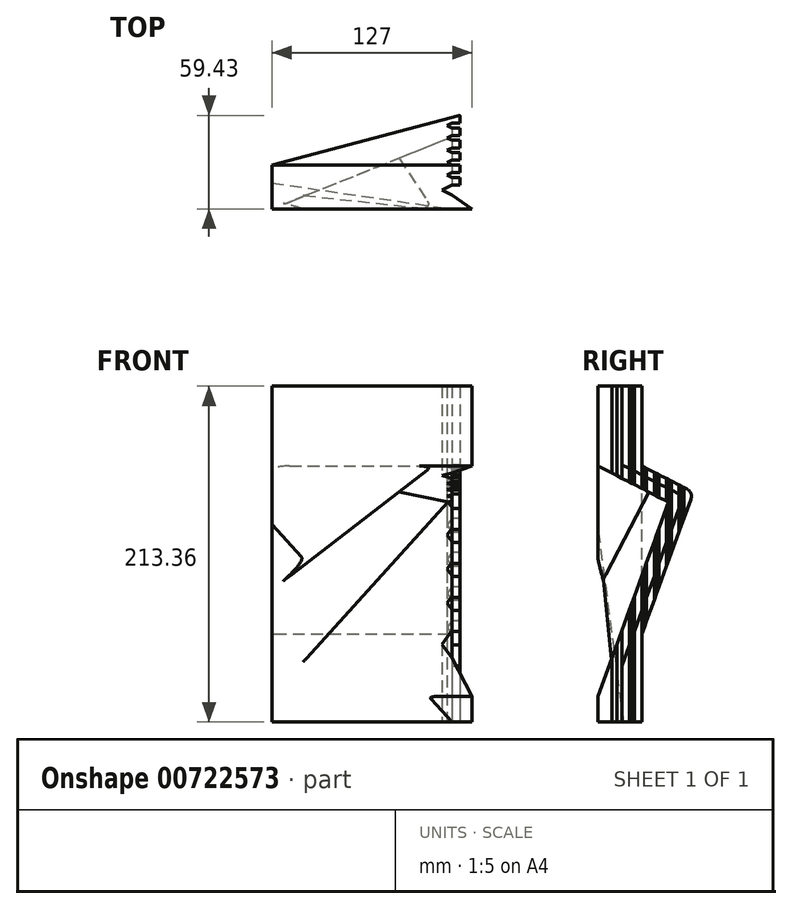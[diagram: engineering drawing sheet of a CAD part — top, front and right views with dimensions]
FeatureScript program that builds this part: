
annotation { "Feature Type Name" : "Feature", "Feature Type Description" : "" }
export const myFeature = defineFeature(function(context is Context, id is Id, definition is map)
    precondition{}
    {
        {
            var Q0;
            Q0=qCreatedBy(makeId("Top.planeOp"),FACE);
            var sketch = newSketch(context, id + "F0", { "sketchPlane" : qUnion([Q0])});
            skLineSegment(sketch, "E0", {"start": v(0, 6.35) * mm, "end": v(5.08, 6.35) * mm});
            skLineSegment(sketch, "E1", {"start": v(5.08, 6.35) * mm, "end": v(5.08, 11.18) * mm});
            skLineSegment(sketch, "E2", {"start": v(5.08, 11.18) * mm, "end": v(0, 11.18) * mm});
            skLineSegment(sketch, "E3", {"start": v(0, 11.18) * mm, "end": v(0, 14.22) * mm});
            skLineSegment(sketch, "E4", {"start": v(0, 14.22) * mm, "end": v(5.08, 14.22) * mm});
            skLineSegment(sketch, "E5", {"start": v(5.08, 14.22) * mm, "end": v(5.08, 19.05) * mm});
            skLineSegment(sketch, "E6", {"start": v(5.08, 19.05) * mm, "end": v(0, 19.05) * mm});
            skLineSegment(sketch, "E7", {"start": v(0, 19.05) * mm, "end": v(0, 22.1) * mm});
            skLineSegment(sketch, "E8", {"start": v(0, 22.1) * mm, "end": v(5.08, 22.1) * mm});
            skLineSegment(sketch, "E9", {"start": v(5.08, 22.1) * mm, "end": v(5.08, 26.92) * mm});
            skLineSegment(sketch, "E10", {"start": v(5.08, 26.92) * mm, "end": v(0, 26.92) * mm});
            skLineSegment(sketch, "E11", {"start": v(0, 26.92) * mm, "end": v(0, 29.97) * mm});
            skLineSegment(sketch, "E12", {"start": v(0, 29.97) * mm, "end": v(5.08, 29.97) * mm});
            skLineSegment(sketch, "E13", {"start": v(5.08, 29.97) * mm, "end": v(5.08, 34.8) * mm});
            skLineSegment(sketch, "E14", {"start": v(5.08, 34.8) * mm, "end": v(0, 34.8) * mm});
            skLineSegment(sketch, "E15", {"start": v(0, 34.8) * mm, "end": v(0, 37.85) * mm});
            skLineSegment(sketch, "E16", {"start": v(0, 37.85) * mm, "end": v(5.08, 37.85) * mm});
            skLineSegment(sketch, "E17", {"start": v(5.08, 37.85) * mm, "end": v(5.08, 42.67) * mm});
            skLineSegment(sketch, "E18", {"start": v(5.08, 42.67) * mm, "end": v(0, 42.67) * mm});
            skLineSegment(sketch, "E19", {"start": v(-114.3, 0) * mm, "end": v(0, 0) * mm});
            skLineSegment(sketch, "E20", {"start": v(0, 0) * mm, "end": v(0, 6.35) * mm});
            skLineSegment(sketch, "E21", {"start": v(0, 42.67) * mm, "end": v(0, 45.72) * mm});
            skLineSegment(sketch, "E22", {"start": v(-114.3, 53.6) * mm, "end": v(-114.3, 0) * mm});
            skLineSegment(sketch, "E23", {"start": v(0, 45.72) * mm, "end": v(5.08, 45.72) * mm});
            skLineSegment(sketch, "E24", {"start": v(5.08, 45.72) * mm, "end": v(5.08, 50.55) * mm});
            skLineSegment(sketch, "E25", {"start": v(5.08, 50.55) * mm, "end": v(0, 50.55) * mm});
            skLineSegment(sketch, "E26", {"start": v(0, 50.55) * mm, "end": v(0, 53.6) * mm});
            skLineSegment(sketch, "E27", {"start": v(0, 53.6) * mm, "end": v(-114.3, 53.6) * mm});
            skLineSegment(sketch, "E28", {"start": v(0, 0) * mm, "end": v(0, -8.89) * mm});
            skLineSegment(sketch, "E29", {"start": v(0, -8.89) * mm, "end": v(-114.3, -8.9) * mm});
            skLineSegment(sketch, "E30", {"start": v(-114.3, -8.9) * mm, "end": v(-114.3, 0) * mm});
            skLineSegment(sketch, "E31", {"start": v(0, -8.89) * mm, "end": v(12.7, -8.89) * mm});
            skLineSegment(sketch, "E32", {"start": v(12.7, -8.89) * mm, "end": v(0, 0) * mm});
            skLineSegment(sketch, "E33", {"start": v(0, 0) * mm, "end": v(-6.35, 3.17) * mm});
            skLineSegment(sketch, "E34", {"start": v(-6.35, 3.18) * mm, "end": v(0, 6.35) * mm});
            skLineSegment(sketch, "E35", {"start": v(0, 11.18) * mm, "end": v(-3.05, 12.7) * mm});
            skLineSegment(sketch, "E36", {"start": v(-3.05, 12.7) * mm, "end": v(0, 14.22) * mm});
            skLineSegment(sketch, "E37", {"start": v(0, 19.05) * mm, "end": v(-3.05, 20.57) * mm});
            skPoint(sketch, "E37.endSnap0", {"position": v(0, 20.57) * mm});
            skLineSegment(sketch, "E38", {"start": v(-3.05, 20.57) * mm, "end": v(0, 22.1) * mm});
            skLineSegment(sketch, "E39", {"start": v(0, 26.92) * mm, "end": v(-3.05, 28.45) * mm});
            skLineSegment(sketch, "E40", {"start": v(-3.05, 28.45) * mm, "end": v(0, 29.97) * mm});
            skLineSegment(sketch, "E41", {"start": v(0, 34.8) * mm, "end": v(-3.05, 36.32) * mm});
            skLineSegment(sketch, "E42", {"start": v(-3.05, 36.32) * mm, "end": v(0, 37.85) * mm});
            skLineSegment(sketch, "E43", {"start": v(0, 42.67) * mm, "end": v(-3.05, 44.2) * mm});
            skPoint(sketch, "E43.endSnap0", {"position": v(0, 44.2) * mm});
            skLineSegment(sketch, "E44", {"start": v(-3.05, 44.2) * mm, "end": v(0, 45.72) * mm});
            skLineSegment(sketch, "E45", {"start": v(0, 50.55) * mm, "end": v(-6.41, 53.6) * mm});
            skSolve(sketch);
        }
        {
            var Q0;
            Q0=makeQuery(id+"F0.imprint","IMPRINT",FACE,{"disambiguationData":[TD([[makeQuery(id+"F0.imprint","IMPRINT",EDGE,{"derivedFrom":sQuery(id+"F0.wireOp",EDGE,"E0")}),1.0]])]});
            var Q1;
            Q1=makeQuery(id+"F0.imprint","IMPRINT",FACE,{"disambiguationData":[TD([[makeQuery(id+"F0.imprint","IMPRINT",EDGE,{"derivedFrom":sQuery(id+"F0.wireOp",EDGE,"E19")}),-1.0]])]});
            var Q2;
            Q2=makeQuery(id+"F0.imprint","IMPRINT",FACE,{"disambiguationData":[TD([[makeQuery(id+"F0.imprint","IMPRINT",EDGE,{"derivedFrom":sQuery(id+"F0.wireOp",EDGE,"E28")}),1.0]])]});
            var Q3;
            Q3=qSketchRegion(id+"F4",true);
            extrude(context, id + "F1", {"entities" : qUnion([Q0, Q1, Q2, Q3]), "depth" : 172.72 * mm, "hasSecondDirection" : true, "secondDirectionOppositeDirection" : true, "secondDirectionDepth" : 40.64 * mm});
        }
        {
            var Q0;
            Q0=makeQuery(id+"F1.opExtrude","SWEPT_FACE",FACE,{"disambiguationData":[OSD([sQuery(id+"F0.wireOp",EDGE,"E22")])]});
            var sketch = newSketch(context, id + "F2", { "sketchPlane" : qUnion([Q0])});
            skLineSegment(sketch, "E46", {"start": v(0, 117.47) * mm, "end": v(-36, 99.06) * mm});
            skLineSegment(sketch, "E47", {"start": v(-36, 99.06) * mm, "end": v(0, 0) * mm});
            skLineSegment(sketch, "E48", {"start": v(0, 117.47) * mm, "end": v(8.9, 122.02) * mm});
            skLineSegment(sketch, "E49", {"start": v(8.89, 122.02) * mm, "end": v(8.89, -24.46) * mm});
            skLineSegment(sketch, "E50", {"start": v(8.9, -24.46) * mm, "end": v(0, 0) * mm});
            skSolve(sketch);
        }
        {
            var Q0;
            Q0=qSketchRegion(id+"F2",true);
            extrude(context, id + "F3", {"entities" : qUnion([Q0]), "operationType" : NewBodyOperationType.REMOVE, "endBound" : BoundingType.THROUGH_ALL, "oppositeDirection" : true, "depth" : 25.4 * mm});
        }
        {
            var Q0;
            {var subQ2=sQuery(id+"F0.wireOp",EDGE,"E1");Q0=makeQuery(id+"F3.boolean.opBoolean","SPLIT",FACE,{"disambiguationData":[TD([makeQuery(id+"F3.opExtrude","SWEPT_FACE",FACE,{"disambiguationData":[OSD([sQuery(id+"F2.wireOp",EDGE,"E46")])]})])],"derivedFrom":makeQuery(id+"F1.opExtrude","SWEPT_FACE",FACE,{"disambiguationData":[OSD([subQ2])]})});}
            var sketch = newSketch(context, id + "F4", { "sketchPlane" : qUnion([Q0])});
            skLineSegment(sketch, "E51.0", {"start": v(0, 117.47) * mm, "end": v(36, 99.06) * mm});
            skLineSegment(sketch, "E52.0", {"start": v(36, 99.06) * mm, "end": v(0, 0) * mm});
            skLineSegment(sketch, "E53", {"start": v(0, 117.47) * mm, "end": v(0, 126.03) * mm});
            skLineSegment(sketch, "E54", {"start": v(0, 126.03) * mm, "end": v(45.46, 102.78) * mm});
            skLineSegment(sketch, "E55", {"start": v(45.46, 102.78) * mm, "end": v(0, -22.3) * mm});
            skLineSegment(sketch, "E56", {"start": v(0, -22.3) * mm, "end": v(0, 0) * mm});
            skSolve(sketch);
        }
        {
            var Q0;
            Q0=qSketchRegion(id+"F4",true);
            var Q1;
            {var subQ1=sQuery(id+"F0.wireOp",EDGE,"E3");Q1=makeQuery(id+"F3.boolean.opBoolean","SPLIT",FACE,{"disambiguationData":[TD([makeQuery(id+"F3.opExtrude","SWEPT_FACE",FACE,{"disambiguationData":[OSD([sQuery(id+"F2.wireOp",EDGE,"E46")])]})])],"derivedFrom":makeQuery(id+"F1.opExtrude","SWEPT_FACE",FACE,{"disambiguationData":[OSD([subQ1])]})});}
            var Q2;
            Q2=makeQuery(id+"F3.boolean.opBoolean","INTERSECT",VERTEX,{"derivedFrom":[makeQuery(id+"F1.opExtrude","SWEPT_FACE",FACE,{"disambiguationData":[OSD([sQuery(id+"F0.wireOp",EDGE,"E0")])]}),makeQuery(id+"F1.opExtrude","SWEPT_FACE",FACE,{"disambiguationData":[OSD([sQuery(id+"F0.wireOp",EDGE,"E34")])]}),makeQuery(id+"F3.opExtrude","SWEPT_FACE",FACE,{"disambiguationData":[OSD([sQuery(id+"F2.wireOp",EDGE,"E46"),sQuery(id+"F2.wireOp",EDGE,"E48")])]})]});
            extrude(context, id + "F5", {"entities" : qUnion([Q0]), "operationType" : NewBodyOperationType.REMOVE, "endBound" : BoundingType.UP_TO_VERTEX, "oppositeDirection" : true, "endBoundEntityFace" : qUnion([Q1]), "endBoundEntityVertex" : qUnion([Q2]), "depth" : 25.4 * mm});
        }
        {
            var Q0;
            {var subQ1=sQuery(id+"F0.wireOp",EDGE,"E5");Q0=makeQuery(id+"F3.boolean.opBoolean","SPLIT",FACE,{"disambiguationData":[TD([makeQuery(id+"F3.opExtrude","SWEPT_FACE",FACE,{"disambiguationData":[OSD([sQuery(id+"F2.wireOp",EDGE,"E46")])]})])],"derivedFrom":makeQuery(id+"F1.opExtrude","SWEPT_FACE",FACE,{"disambiguationData":[OSD([subQ1])]})});}
            var sketch = newSketch(context, id + "F6", { "sketchPlane" : qUnion([Q0])});
            skLineSegment(sketch, "E57", {"start": v(19.05, 122) * mm, "end": v(53.6, 104.33) * mm});
            skLineSegment(sketch, "E58", {"start": v(53.6, 104.33) * mm, "end": v(53.6, 172.72) * mm});
            skLineSegment(sketch, "E59", {"start": v(53.6, 172.72) * mm, "end": v(19.05, 172.72) * mm});
            skLineSegment(sketch, "E60", {"start": v(19.05, 172.72) * mm, "end": v(19.05, 122) * mm});
            skSolve(sketch);
        }
        {
            var Q0;
            Q0=qSketchRegion(id+"F6",true);
            var Q1;
            {var subQ2=makeQuery(id+"F3.opExtrude","SWEPT_FACE",FACE,{"disambiguationData":[OSD([sQuery(id+"F2.wireOp",EDGE,"E46")])]});var subQ5=sQuery(id+"F0.wireOp",EDGE,"E21");var subQ6=sQuery(id+"F0.wireOp",EDGE,"E20");var subQ11=sQuery(id+"F0.wireOp",EDGE,"E15");var subQ15=sQuery(id+"F0.wireOp",EDGE,"E11");var subQ19=sQuery(id+"F0.wireOp",EDGE,"E7");var subQ23=sQuery(id+"F0.wireOp",EDGE,"E3");var subQ28=makeQuery(id+"F1.opExtrude","SWEPT_FACE",FACE,{"disambiguationData":[OSD([subQ6])]});var subQ30=makeQuery(id+"F3.opExtrude","SWEPT_FACE",FACE,{"disambiguationData":[OSD([sQuery(id+"F2.wireOp",EDGE,"E47")])]});var subQ33=makeQuery(id+"F1.opExtrude","SWEPT_FACE",FACE,{"disambiguationData":[OSD([subQ11])]});var subQ36=makeQuery(id+"F1.opExtrude","SWEPT_FACE",FACE,{"disambiguationData":[OSD([subQ15])]});var subQ39=makeQuery(id+"F1.opExtrude","SWEPT_FACE",FACE,{"disambiguationData":[OSD([subQ19])]});var subQ42=makeQuery(id+"F1.opExtrude","SWEPT_FACE",FACE,{"disambiguationData":[OSD([subQ23])]});Q1=makeQuery(id+"F5.boolean.opBoolean","MERGE",FACE,{"derivedFrom":[makeQuery(id+"F1.opExtrude","SWEPT_FACE",FACE,{"disambiguationData":[OSD([subQ5])]}),makeQuery(id+"F3.boolean.opBoolean","SPLIT",FACE,{"disambiguationData":[TD([subQ30])],"derivedFrom":subQ42}),makeQuery(id+"F3.boolean.opBoolean","SPLIT",FACE,{"disambiguationData":[TD([subQ2])],"derivedFrom":subQ42}),makeQuery(id+"F3.boolean.opBoolean","SPLIT",FACE,{"disambiguationData":[TD([subQ30])],"derivedFrom":subQ39}),makeQuery(id+"F3.boolean.opBoolean","SPLIT",FACE,{"disambiguationData":[TD([subQ2])],"derivedFrom":subQ39}),makeQuery(id+"F3.boolean.opBoolean","SPLIT",FACE,{"disambiguationData":[TD([subQ30])],"derivedFrom":subQ36}),makeQuery(id+"F3.boolean.opBoolean","SPLIT",FACE,{"disambiguationData":[TD([subQ2])],"derivedFrom":subQ36}),makeQuery(id+"F3.boolean.opBoolean","SPLIT",FACE,{"disambiguationData":[TD([subQ30])],"derivedFrom":subQ33}),makeQuery(id+"F3.boolean.opBoolean","SPLIT",FACE,{"disambiguationData":[TD([subQ2])],"derivedFrom":subQ33}),makeQuery(id+"F3.boolean.opBoolean","SPLIT",FACE,{"disambiguationData":[TD([subQ30])],"derivedFrom":subQ28}),makeQuery(id+"F3.boolean.opBoolean","SPLIT",FACE,{"disambiguationData":[TD([subQ2])],"derivedFrom":subQ28}),makeQuery(id+"F5.opExtrude","CAP_FACE",FACE,{"disambiguationData":[OSD([sQuery(id+"F4.wireOp",EDGE,"r30LgNDP-MDBT-sFvh-t1dZ-1n8YGESDknUK"),sQuery(id+"F4.wireOp",EDGE,"V1CvVt0y-FSvr-zVPq-IvBo-Jav4YfUzxSMJ"),sQuery(id+"F4.wireOp",EDGE,"HjBI8CUT-Bw1e-LJHy-u5lc-1jVyPCsQLfoZ"),sQuery(id+"F4.wireOp",EDGE,"4X511eva-4H63-5xgH-bIHv-RUgGeS7ULBsc")])],"isStart":false})]});}
            extrude(context, id + "F7", {"entities" : qUnion([Q0]), "operationType" : NewBodyOperationType.REMOVE, "endBound" : BoundingType.THROUGH_ALL, "oppositeDirection" : true, "endBoundEntityFace" : qUnion([Q1]), "depth" : 25.4 * mm});
        }
        {
            var Q0;
            {var subQ1=sQuery(id+"F0.wireOp",EDGE,"E5");Q0=makeQuery(id+"F3.boolean.opBoolean","SPLIT",FACE,{"disambiguationData":[TD([makeQuery(id+"F3.opExtrude","SWEPT_FACE",FACE,{"disambiguationData":[OSD([sQuery(id+"F2.wireOp",EDGE,"E47")])]})])],"derivedFrom":makeQuery(id+"F1.opExtrude","SWEPT_FACE",FACE,{"disambiguationData":[OSD([subQ1])]})});}
            var sketch = newSketch(context, id + "F8", { "sketchPlane" : qUnion([Q0])});
            skLineSegment(sketch, "E61", {"start": v(19.05, 15.24) * mm, "end": v(53.6, 110.3) * mm});
            skLineSegment(sketch, "E62", {"start": v(53.6, 110.3) * mm, "end": v(53.6, -40.64) * mm});
            skLineSegment(sketch, "E63", {"start": v(53.6, -40.64) * mm, "end": v(19.05, -40.64) * mm});
            skLineSegment(sketch, "E64", {"start": v(19.05, -40.64) * mm, "end": v(19.05, 15.24) * mm});
            skSolve(sketch);
        }
        {
            var Q0;
            Q0=qSketchRegion(id+"F8",true);
            extrude(context, id + "F9", {"entities" : qUnion([Q0]), "operationType" : NewBodyOperationType.REMOVE, "endBound" : BoundingType.THROUGH_ALL, "oppositeDirection" : true, "depth" : 25.4 * mm});
        }
        {
            var Q0;
            Q0=qCreatedBy(makeId("Top.planeOp"),FACE);
            var sketch = newSketch(context, id + "F10", { "sketchPlane" : qUnion([Q0])});
            skLineSegment(sketch, "E65", {"start": v(-114.3, 36) * mm, "end": v(-2.4, 36) * mm});
            skLineSegment(sketch, "E66", {"start": v(-2.4, 36) * mm, "end": v(-114.3, -8.9) * mm});
            skLineSegment(sketch, "E67", {"start": v(-114.3, -8.9) * mm, "end": v(-114.3, 36) * mm});
            skSolve(sketch);
        }
        {
            var Q0;
            Q0=makeQuery(id+"F10.imprint","IMPRINT",FACE,{"disambiguationData":[TD([[makeQuery(id+"F10.imprint","IMPRINT",EDGE,{"derivedFrom":sQuery(id+"F10.wireOp",EDGE,"E65")}),-1.0]])]});
            var Q1;
            Q1=makeQuery(id+"F3.boolean.opBoolean","COPY",FACE,{"derivedFrom":makeQuery(id+"F3.opExtrude","SWEPT_FACE",FACE,{"disambiguationData":[OSD([sQuery(id+"F2.wireOp",EDGE,"E46"),sQuery(id+"F2.wireOp",EDGE,"E48")])]})});
            var Q2;
            Q2=makeQuery(id+"F3.boolean.opBoolean","COPY",FACE,{"derivedFrom":makeQuery(id+"F3.opExtrude","SWEPT_FACE",FACE,{"disambiguationData":[OSD([sQuery(id+"F2.wireOp",EDGE,"E47"),sQuery(id+"F2.wireOp",EDGE,"E50")])]})});
            extrude(context, id + "F11", {"entities" : qUnion([Q0]), "operationType" : NewBodyOperationType.ADD, "endBound" : BoundingType.UP_TO_SURFACE, "endBoundEntityFace" : qUnion([Q1]), "depth" : 25.4 * mm, "hasSecondDirection" : true, "secondDirectionBound" : SecondDirectionBoundingType.UP_TO_SURFACE, "secondDirectionOppositeDirection" : true, "secondDirectionBoundEntityFace" : qUnion([Q2]), "secondDirectionDepth" : 25.4 * mm});
        }
        {
            var Q0;
            Q0=makeQuery(id+"F1.opExtrude","CAP_FACE",FACE,{"disambiguationData":[OSD([sQuery(id+"F0.wireOp",EDGE,"E0"),sQuery(id+"F0.wireOp",EDGE,"E1"),sQuery(id+"F0.wireOp",EDGE,"E2"),sQuery(id+"F0.wireOp",EDGE,"E3"),sQuery(id+"F0.wireOp",EDGE,"E4"),sQuery(id+"F0.wireOp",EDGE,"E5"),sQuery(id+"F0.wireOp",EDGE,"E6"),sQuery(id+"F0.wireOp",EDGE,"E7"),sQuery(id+"F0.wireOp",EDGE,"E8"),sQuery(id+"F0.wireOp",EDGE,"E9"),sQuery(id+"F0.wireOp",EDGE,"E10"),sQuery(id+"F0.wireOp",EDGE,"E11"),sQuery(id+"F0.wireOp",EDGE,"E12"),sQuery(id+"F0.wireOp",EDGE,"E13"),sQuery(id+"F0.wireOp",EDGE,"E14"),sQuery(id+"F0.wireOp",EDGE,"E15"),sQuery(id+"F0.wireOp",EDGE,"E16"),sQuery(id+"F0.wireOp",EDGE,"E17"),sQuery(id+"F0.wireOp",EDGE,"E18"),sQuery(id+"F0.wireOp",EDGE,"E20"),sQuery(id+"F0.wireOp",EDGE,"E21"),sQuery(id+"F0.wireOp",EDGE,"E22"),sQuery(id+"F0.wireOp",EDGE,"E23"),sQuery(id+"F0.wireOp",EDGE,"E24"),sQuery(id+"F0.wireOp",EDGE,"E25"),sQuery(id+"F0.wireOp",EDGE,"E26"),sQuery(id+"F0.wireOp",EDGE,"E27"),sQuery(id+"F0.wireOp",EDGE,"E29"),sQuery(id+"F0.wireOp",EDGE,"E30"),sQuery(id+"F0.wireOp",EDGE,"E31"),sQuery(id+"F0.wireOp",EDGE,"E32")])],"isStart":false});
            var sketch = newSketch(context, id + "F12", { "sketchPlane" : qUnion([Q0])});
            skLineSegment(sketch, "E68", {"start": v(-114.3, 19.05) * mm, "end": v(5.08, 50.55) * mm});
            skLineSegment(sketch, "E69", {"start": v(5.08, 50.55) * mm, "end": v(-114.3, 50.55) * mm});
            skLineSegment(sketch, "E70", {"start": v(-114.3, 50.55) * mm, "end": v(-114.3, 19.05) * mm});
            skLineSegment(sketch, "E71", {"start": v(5.08, 50.55) * mm, "end": v(14.04, 52.91) * mm});
            skLineSegment(sketch, "E72", {"start": v(14.04, 52.91) * mm, "end": v(-114.3, 52.91) * mm});
            skLineSegment(sketch, "E73", {"start": v(-114.3, 52.91) * mm, "end": v(-114.3, 50.55) * mm});
            skSolve(sketch);
        }
        {
            var Q0;
            Q0=qSketchRegion(id+"F12",true);
            extrude(context, id + "F13", {"entities" : qUnion([Q0]), "operationType" : NewBodyOperationType.REMOVE, "endBound" : BoundingType.THROUGH_ALL, "oppositeDirection" : true, "depth" : 25.4 * mm});
        }
        {
            var Q0;
            Q0=makeQuery(id+"F13.boolean.opBoolean","INTERSECT",EDGE,{"derivedFrom":[makeQuery(id+"F9.boolean.opBoolean","COPY",FACE,{"derivedFrom":makeQuery(id+"F9.opExtrude","SWEPT_FACE",FACE,{"disambiguationData":[OSD([sQuery(id+"F8.wireOp",EDGE,"E61")])]})}),makeQuery(id+"F13.opExtrude","SWEPT_FACE",FACE,{"disambiguationData":[OSD([sQuery(id+"F12.wireOp",EDGE,"E68"),sQuery(id+"F12.wireOp",EDGE,"E71")])]})]});
            var Q1;
            Q1=makeQuery(id+"F13.boolean.opBoolean","INTERSECT",EDGE,{"derivedFrom":[makeQuery(id+"F7.boolean.opBoolean","COPY",FACE,{"derivedFrom":makeQuery(id+"F7.opExtrude","SWEPT_FACE",FACE,{"disambiguationData":[OSD([sQuery(id+"F6.wireOp",EDGE,"E57")])]})}),makeQuery(id+"F13.opExtrude","SWEPT_FACE",FACE,{"disambiguationData":[OSD([sQuery(id+"F12.wireOp",EDGE,"E68"),sQuery(id+"F12.wireOp",EDGE,"E71")])]})]});
            fillet(context, id + "F14", {"entities" : qUnion([Q0, Q1]), "radius" : 5.08 * mm, "tangentPropagation" : true, "allowEdgeOverflow" : false});
        }
        {
            var Q0;
            {var subQ1=sQuery(id+"F0.wireOp",EDGE,"E31");var subQ3=sQuery(id+"F0.wireOp",EDGE,"E29");Q0=makeQuery(id+"F3.boolean.opBoolean","SPLIT",FACE,{"disambiguationData":[TD([makeQuery(id+"F3.opExtrude","SWEPT_FACE",FACE,{"disambiguationData":[OSD([sQuery(id+"F2.wireOp",EDGE,"E46"),sQuery(id+"F2.wireOp",EDGE,"E48")])]})])],"derivedFrom":makeQuery(id+"F1.opExtrude","SWEPT_FACE",FACE,{"disambiguationData":[OSD([subQ3,subQ1])]})});}
            var sketch = newSketch(context, id + "F15", { "sketchPlane" : qUnion([Q0])});
            skLineSegment(sketch, "E74", {"start": v(-12.26, 122.02) * mm, "end": v(-114.3, 43.28) * mm});
            skLineSegment(sketch, "E75", {"start": v(-114.3, 43.28) * mm, "end": v(-114.3, 122.02) * mm});
            skLineSegment(sketch, "E76", {"start": v(-114.3, 122.02) * mm, "end": v(-12.26, 122.02) * mm});
            skSolve(sketch);
        }
        {
            var Q0;
            Q0=qSketchRegion(id+"F15",true);
            extrude(context, id + "F16", {"entities" : qUnion([Q0]), "operationType" : NewBodyOperationType.ADD, "endBound" : BoundingType.UP_TO_NEXT, "oppositeDirection" : true, "depth" : 25.4 * mm});
        }
        {
            var Q0;
            Q0=makeQuery(id+"F2.imprint","IMPRINT",FACE,{"disambiguationData":[TD([[makeQuery(id+"F2.imprint","IMPRINT",EDGE,{"derivedFrom":sQuery(id+"F2.wireOp",EDGE,"E46")}),-1.0]])]});
            var sketch = newSketch(context, id + "F17", { "sketchPlane" : qUnion([Q0])});
            skLineSegment(sketch, "E77", {"start": v(-7.62, -40.64) * mm, "end": v(8.89, 84.77) * mm});
            skLineSegment(sketch, "E78", {"start": v(8.89, 84.77) * mm, "end": v(8.9, -40.64) * mm});
            skLineSegment(sketch, "E79", {"start": v(8.9, -40.64) * mm, "end": v(-7.62, -40.64) * mm});
            skSolve(sketch);
        }
        {
            var Q0;
            Q0=makeQuery(id+"F1.opExtrude","CAP_FACE",FACE,{"disambiguationData":[OSD([sQuery(id+"F0.wireOp",EDGE,"E0"),sQuery(id+"F0.wireOp",EDGE,"E1"),sQuery(id+"F0.wireOp",EDGE,"E2"),sQuery(id+"F0.wireOp",EDGE,"E3"),sQuery(id+"F0.wireOp",EDGE,"E4"),sQuery(id+"F0.wireOp",EDGE,"E5"),sQuery(id+"F0.wireOp",EDGE,"E6"),sQuery(id+"F0.wireOp",EDGE,"E7"),sQuery(id+"F0.wireOp",EDGE,"E8"),sQuery(id+"F0.wireOp",EDGE,"E9"),sQuery(id+"F0.wireOp",EDGE,"E10"),sQuery(id+"F0.wireOp",EDGE,"E11"),sQuery(id+"F0.wireOp",EDGE,"E12"),sQuery(id+"F0.wireOp",EDGE,"E13"),sQuery(id+"F0.wireOp",EDGE,"E14"),sQuery(id+"F0.wireOp",EDGE,"E15"),sQuery(id+"F0.wireOp",EDGE,"E16"),sQuery(id+"F0.wireOp",EDGE,"E17"),sQuery(id+"F0.wireOp",EDGE,"E18"),sQuery(id+"F0.wireOp",EDGE,"E20"),sQuery(id+"F0.wireOp",EDGE,"E21"),sQuery(id+"F0.wireOp",EDGE,"E22"),sQuery(id+"F0.wireOp",EDGE,"E23"),sQuery(id+"F0.wireOp",EDGE,"E24"),sQuery(id+"F0.wireOp",EDGE,"E25"),sQuery(id+"F0.wireOp",EDGE,"E26"),sQuery(id+"F0.wireOp",EDGE,"E27"),sQuery(id+"F0.wireOp",EDGE,"E29"),sQuery(id+"F0.wireOp",EDGE,"E30"),sQuery(id+"F0.wireOp",EDGE,"E31"),sQuery(id+"F0.wireOp",EDGE,"E32")])],"isStart":true});
            var sketch = newSketch(context, id + "F18", { "sketchPlane" : qUnion([Q0])});
            skLineSegment(sketch, "E80", {"start": v(0, 8.9) * mm, "end": v(-114.3, -7.62) * mm});
            skSolve(sketch);
        }
        {
            var Q0;
            Q0=qSketchRegion(id+"F17",true);
            var Q1;
            Q1=sQuery(id+"F18.wireOp",EDGE,"E80");
            sweep(context, id + "F19", {"operationType" : NewBodyOperationType.REMOVE, "profiles" : qUnion([Q0]), "path" : qUnion([Q1])});
        }
        {
            var Q0;
            Q0=makeQuery(id+"F19.boolean.opBoolean","INTERSECT",EDGE,{"derivedFrom":[makeQuery(id+"F3.boolean.opBoolean","COPY",FACE,{"derivedFrom":makeQuery(id+"F3.opExtrude","SWEPT_FACE",FACE,{"disambiguationData":[OSD([sQuery(id+"F2.wireOp",EDGE,"E47"),sQuery(id+"F2.wireOp",EDGE,"E50")])]})}),makeQuery(id+"F19.opSweep","SWEPT_FACE",FACE,{"disambiguationData":[OSD([sQuery(id+"F17.wireOp",EDGE,"E77"),sQuery(id+"F18.wireOp",EDGE,"E80")])]})]});
            fillet(context, id + "F20", {"entities" : qUnion([Q0]), "radius" : 5.08 * mm, "tangentPropagation" : true, "allowEdgeOverflow" : false});
        }
        {
            var Q0;
            Q0=makeQuery(id+"F16.opExtrude","CAP_EDGE",EDGE,{"disambiguationData":[OSD([sQuery(id+"F15.wireOp",EDGE,"E74")])],"isStart":true});
            fillet(context, id + "F21", {"entities" : qUnion([Q0]), "radius" : 5.08 * mm, "tangentPropagation" : true, "allowEdgeOverflow" : false});
        }
        {
            var Q0;
            Q0=makeQuery(id+"F19.boolean.opBoolean","INTERSECT",EDGE,{"derivedFrom":[makeQuery(id+"F11.opExtrude","SWEPT_FACE",FACE,{"disambiguationData":[OSD([sQuery(id+"F10.wireOp",EDGE,"E66")])]}),makeQuery(id+"F19.opSweep","SWEPT_FACE",FACE,{"disambiguationData":[OSD([sQuery(id+"F17.wireOp",EDGE,"E77"),sQuery(id+"F18.wireOp",EDGE,"E80")])]})]});
            fillet(context, id + "F22", {"entities" : qUnion([Q0]), "radius" : 5.08 * mm, "tangentPropagation" : true, "allowEdgeOverflow" : false});
        }
    });
